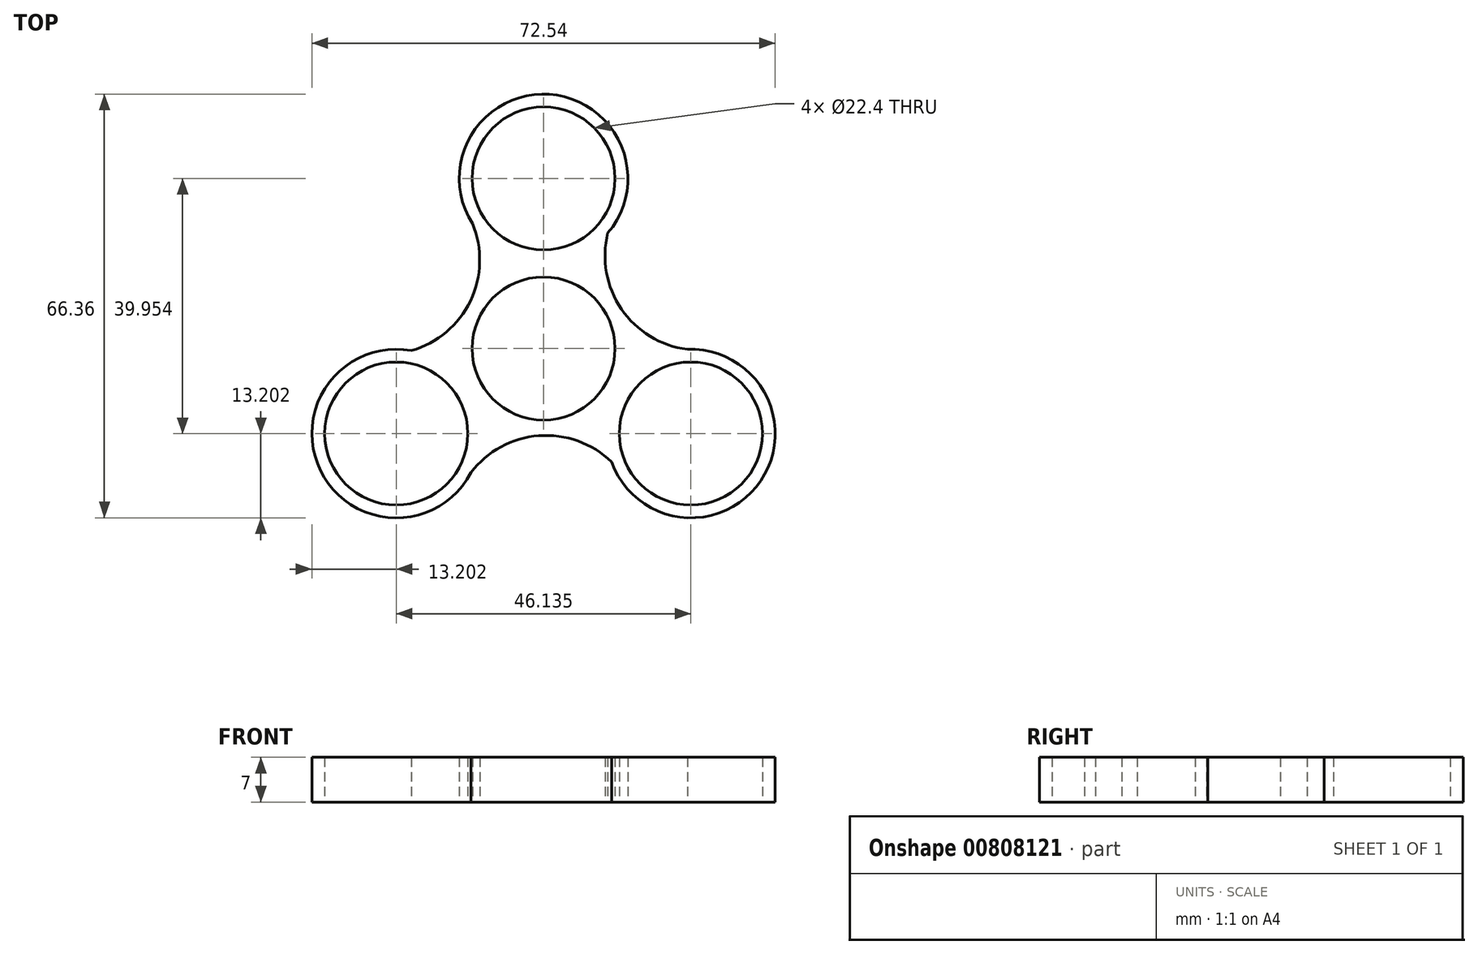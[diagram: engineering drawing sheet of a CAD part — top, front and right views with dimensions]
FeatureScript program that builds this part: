
annotation { "Feature Type Name" : "Feature", "Feature Type Description" : "" }
export const myFeature = defineFeature(function(context is Context, id is Id, definition is map)
    precondition{}
    {
        {
            var Q0;
            Q0=qCreatedBy(makeId("Top.planeOp"),FACE);
            var sketch = newSketch(context, id + "F0", { "sketchPlane" : qUnion([Q0])});
            skCircle(sketch, "E0", {"center": v(0, 0) * mm, "radius": 11.2 * mm});
            skCircle(sketch, "E1", {"center": v(0, 26.64) * mm, "radius": 11.2 * mm});
            skArc(sketch, "E2", {"start": v(10.06, 18.09) * mm, "mid": v(0.91, 39.8) * mm, "end": v(-11.14, 19.56) * mm});
            skArc(sketch, "E3.1.0", {"start": v(-20.7, -0.33) * mm, "mid": v(-34.93, -19.11) * mm, "end": v(-11.37, -19.43) * mm});
            skCircle(sketch, "E3.1.1", {"center": v(-23.07, -13.32) * mm, "radius": 11.2 * mm});
            skArc(sketch, "E3.2.0", {"start": v(10.64, -17.75) * mm, "mid": v(34.01, -20.7) * mm, "end": v(22.51, -0.13) * mm});
            skCircle(sketch, "E3.2.1", {"center": v(23.07, -13.32) * mm, "radius": 11.2 * mm});
            skLineSegment(sketch, "E4", {"start": v(9.7, 5.6) * mm, "end": v(11.8, 6.8) * mm, "construction": true});
            skArc(sketch, "E5", {"start": v(10.06, 18.09) * mm, "mid": v(12.2, 6.18) * mm, "end": v(22.51, -0.13) * mm});
            skArc(sketch, "E6.1.0", {"start": v(-20.7, -0.33) * mm, "mid": v(-11.45, 7.47) * mm, "end": v(-11.14, 19.56) * mm});
            skArc(sketch, "E6.2.0", {"start": v(10.64, -17.75) * mm, "mid": v(-0.74, -13.65) * mm, "end": v(-11.37, -19.43) * mm});
            skSolve(sketch);
        }
        {
            var Q0;
            Q0=makeQuery(id+"F0.imprint","IMPRINT",FACE,{"disambiguationData":[TD([[makeQuery(id+"F0.imprint","IMPRINT",EDGE,{"derivedFrom":sQuery(id+"F0.wireOp",EDGE,"E0")}),-1.0]])]});
            extrude(context, id + "F1", {"entities" : qUnion([Q0]), "depth" : 7 * mm, "offsetDistance" : 25 * mm});
        }
    });
